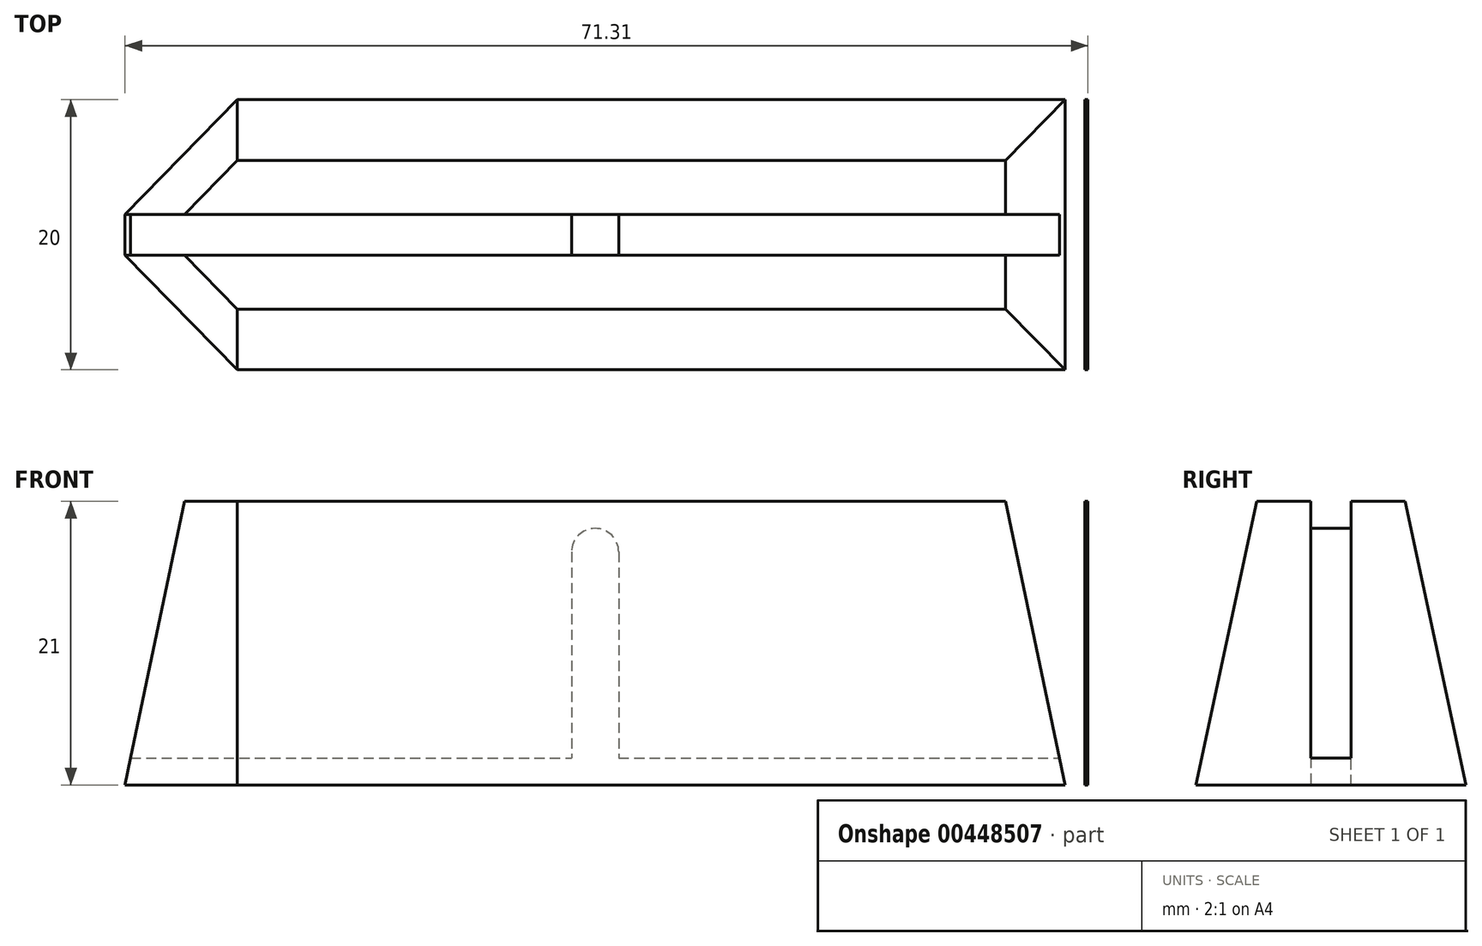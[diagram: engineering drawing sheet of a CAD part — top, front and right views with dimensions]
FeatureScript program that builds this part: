
annotation { "Feature Type Name" : "Feature", "Feature Type Description" : "" }
export const myFeature = defineFeature(function(context is Context, id is Id, definition is map)
    precondition{}
    {
        {
            var Q0;
            Q0=qCreatedBy(makeId("Top.planeOp"),FACE);
            var sketch = newSketch(context, id + "F0", { "sketchPlane" : qUnion([Q0])});
            skLineSegment(sketch, "E0.bottom", {"start": v(0, 0) * mm, "end": v(73, 0) * mm});
            skLineSegment(sketch, "E0.top", {"start": v(0, 20) * mm, "end": v(73, 20) * mm});
            skLineSegment(sketch, "E0.left", {"start": v(0, 0) * mm, "end": v(0, 20) * mm});
            skLineSegment(sketch, "E0.right", {"start": v(73, 0) * mm, "end": v(73, 20) * mm});
            skSolve(sketch);
        }
        {
            var Q0;
            Q0=makeQuery(id+"F0.imprint","IMPRINT",FACE,{"disambiguationData":[TD([[makeQuery(id+"F0.imprint","IMPRINT",EDGE,{"derivedFrom":sQuery(id+"F0.wireOp",EDGE,"E0.bottom")}),1.0]])]});
            extrude(context, id + "F1", {"entities" : qUnion([Q0]), "depth" : 21 * mm});
        }
        {
            var Q0;
            Q0=makeQuery(id+"F1.opExtrude","SWEPT_FACE",FACE,{"disambiguationData":[OSD([sQuery(id+"F0.wireOp",EDGE,"E0.right")])]});
            var sketch = newSketch(context, id + "F2", { "sketchPlane" : qUnion([Q0])});
            skLineSegment(sketch, "E1", {"start": v(15.5, 21) * mm, "end": v(20, 0) * mm});
            skLineSegment(sketch, "E2", {"start": v(20, 0) * mm, "end": v(20, 21) * mm});
            skLineSegment(sketch, "E3", {"start": v(20, 21) * mm, "end": v(15.5, 21) * mm});
            skLineSegment(sketch, "E4.bottom", {"start": v(8.5, 21) * mm, "end": v(11.5, 21) * mm});
            skLineSegment(sketch, "E4.top", {"start": v(8.5, 2) * mm, "end": v(11.5, 2) * mm});
            skLineSegment(sketch, "E4.left", {"start": v(8.5, 21) * mm, "end": v(8.5, 2) * mm});
            skLineSegment(sketch, "E4.right", {"start": v(11.5, 21) * mm, "end": v(11.5, 2) * mm});
            skLineSegment(sketch, "E5", {"start": v(0, 21) * mm, "end": v(0, 0) * mm});
            skLineSegment(sketch, "E6", {"start": v(0, 0) * mm, "end": v(4.5, 21) * mm});
            skLineSegment(sketch, "E7", {"start": v(4.5, 21) * mm, "end": v(0, 21) * mm});
            skSolve(sketch);
        }
        {
            var Q0;
            Q0 = qSketchRegion(id + "F2", true);
            extrude(context, id + "F3", {"entities" : qUnion([Q0]), "operationType" : NewBodyOperationType.REMOVE, "endBound" : BoundingType.THROUGH_ALL, "oppositeDirection" : true, "depth" : 25 * mm});
        }
        {
            var Q0;
            Q0=makeQuery(id+"F3.boolean.opBoolean","COPY",FACE,{"derivedFrom":makeQuery(id+"F3.opExtrude","SWEPT_FACE",FACE,{"disambiguationData":[OSD([sQuery(id+"F2.wireOp",EDGE,"E4.top")])]})});
            var sketch = newSketch(context, id + "F4", { "sketchPlane" : qUnion([Q0])});
            skLineSegment(sketch, "E8.bottom", {"start": v(36.5, 11.5) * mm, "end": v(34.75, 11.5) * mm});
            skLineSegment(sketch, "E8.top", {"start": v(36.5, 8.5) * mm, "end": v(34.75, 8.5) * mm});
            skLineSegment(sketch, "E8.left", {"start": v(36.5, 11.5) * mm, "end": v(36.5, 8.5) * mm});
            skLineSegment(sketch, "E8.right", {"start": v(34.75, 11.5) * mm, "end": v(34.75, 8.5) * mm});
            skLineSegment(sketch, "E9.bottom", {"start": v(36.5, 11.5) * mm, "end": v(38.25, 11.5) * mm});
            skLineSegment(sketch, "E9.top", {"start": v(36.5, 8.5) * mm, "end": v(38.25, 8.5) * mm});
            skLineSegment(sketch, "E9.right", {"start": v(38.25, 11.5) * mm, "end": v(38.25, 8.5) * mm});
            skSolve(sketch);
        }
        {
            var Q0;
            Q0 = qSketchRegion(id + "F4", true);
            extrude(context, id + "F5", {"entities" : qUnion([Q0]), "operationType" : NewBodyOperationType.ADD, "depth" : 17 * mm});
        }
        {
            var Q0;
            Q0=makeQuery(id+"F5.opExtrude","CAP_EDGE",EDGE,{"disambiguationData":[OSD([sQuery(id+"F4.wireOp",EDGE,"E9.right")])],"isStart":false});
            var Q1;
            Q1=makeQuery(id+"F5.opExtrude","CAP_EDGE",EDGE,{"disambiguationData":[OSD([sQuery(id+"F4.wireOp",EDGE,"E8.right")])],"isStart":false});
            fillet(context, id + "F6", {"entities" : qUnion([Q0, Q1]), "radius" : 1.75 * mm, "tangentPropagation" : true, "allowEdgeOverflow" : false});
        }
        {
            var Q0;
            Q0=makeQuery(id+"F3.boolean.opBoolean","COPY",EDGE,{"derivedFrom":makeQuery(id+"F3.opExtrude","CAP_EDGE",EDGE,{"disambiguationData":[OSD([sQuery(id+"F2.wireOp",EDGE,"E1")])],"isStart":true})});
            var Q1;
            Q1=makeQuery(id+"F3.boolean.opBoolean","COPY",EDGE,{"derivedFrom":makeQuery(id+"F3.opExtrude","CAP_EDGE",EDGE,{"disambiguationData":[OSD([sQuery(id+"F2.wireOp",EDGE,"E6")])],"isStart":true})});
            var Q2;
            Q2=makeQuery(id+"F3.boolean.opBoolean","INTERSECT",EDGE,{"derivedFrom":[makeQuery(id+"F1.opExtrude","SWEPT_FACE",FACE,{"disambiguationData":[OSD([sQuery(id+"F0.wireOp",EDGE,"E0.left")])]}),makeQuery(id+"F3.opExtrude","SWEPT_FACE",FACE,{"disambiguationData":[OSD([sQuery(id+"F2.wireOp",EDGE,"E1")])]})]});
            var Q3;
            Q3=makeQuery(id+"F3.boolean.opBoolean","INTERSECT",EDGE,{"derivedFrom":[makeQuery(id+"F1.opExtrude","SWEPT_FACE",FACE,{"disambiguationData":[OSD([sQuery(id+"F0.wireOp",EDGE,"E0.left")])]}),makeQuery(id+"F3.opExtrude","SWEPT_FACE",FACE,{"disambiguationData":[OSD([sQuery(id+"F2.wireOp",EDGE,"E6")])]})]});
            chamfer(context, id + "F7", {"entities" : qUnion([Q0, Q1, Q2, Q3]), "width" : 10 * mm, "tangentPropagation" : true});
        }
        {
            var Q0;
            Q0=qCreatedBy(makeId("Front.planeOp"),FACE);
            var sketch = newSketch(context, id + "F8", { "sketchPlane" : qUnion([Q0])});
            skLineSegment(sketch, "E10", {"start": v(6.09, 21) * mm, "end": v(1.69, 0) * mm});
            skLineSegment(sketch, "E11", {"start": v(1.69, 0) * mm, "end": v(0, 0) * mm});
            skLineSegment(sketch, "E12", {"start": v(0, 0) * mm, "end": v(0, 21) * mm});
            skLineSegment(sketch, "E13", {"start": v(0, 21) * mm, "end": v(6.09, 21) * mm});
            skLineSegment(sketch, "E14", {"start": v(66.91, 21) * mm, "end": v(71.31, 0) * mm});
            skLineSegment(sketch, "E15", {"start": v(71.31, 0) * mm, "end": v(72.78, 0) * mm});
            skLineSegment(sketch, "E16", {"start": v(72.78, 0) * mm, "end": v(72.78, 21) * mm});
            skLineSegment(sketch, "E17", {"start": v(72.78, 21) * mm, "end": v(66.91, 21) * mm});
            skSolve(sketch);
        }
        {
            var Q0;
            Q0 = qSketchRegion(id + "F8", true);
            extrude(context, id + "F9", {"entities" : qUnion([Q0]), "operationType" : NewBodyOperationType.REMOVE, "endBound" : BoundingType.THROUGH_ALL, "oppositeDirection" : true, "depth" : 25 * mm});
        }
    });
